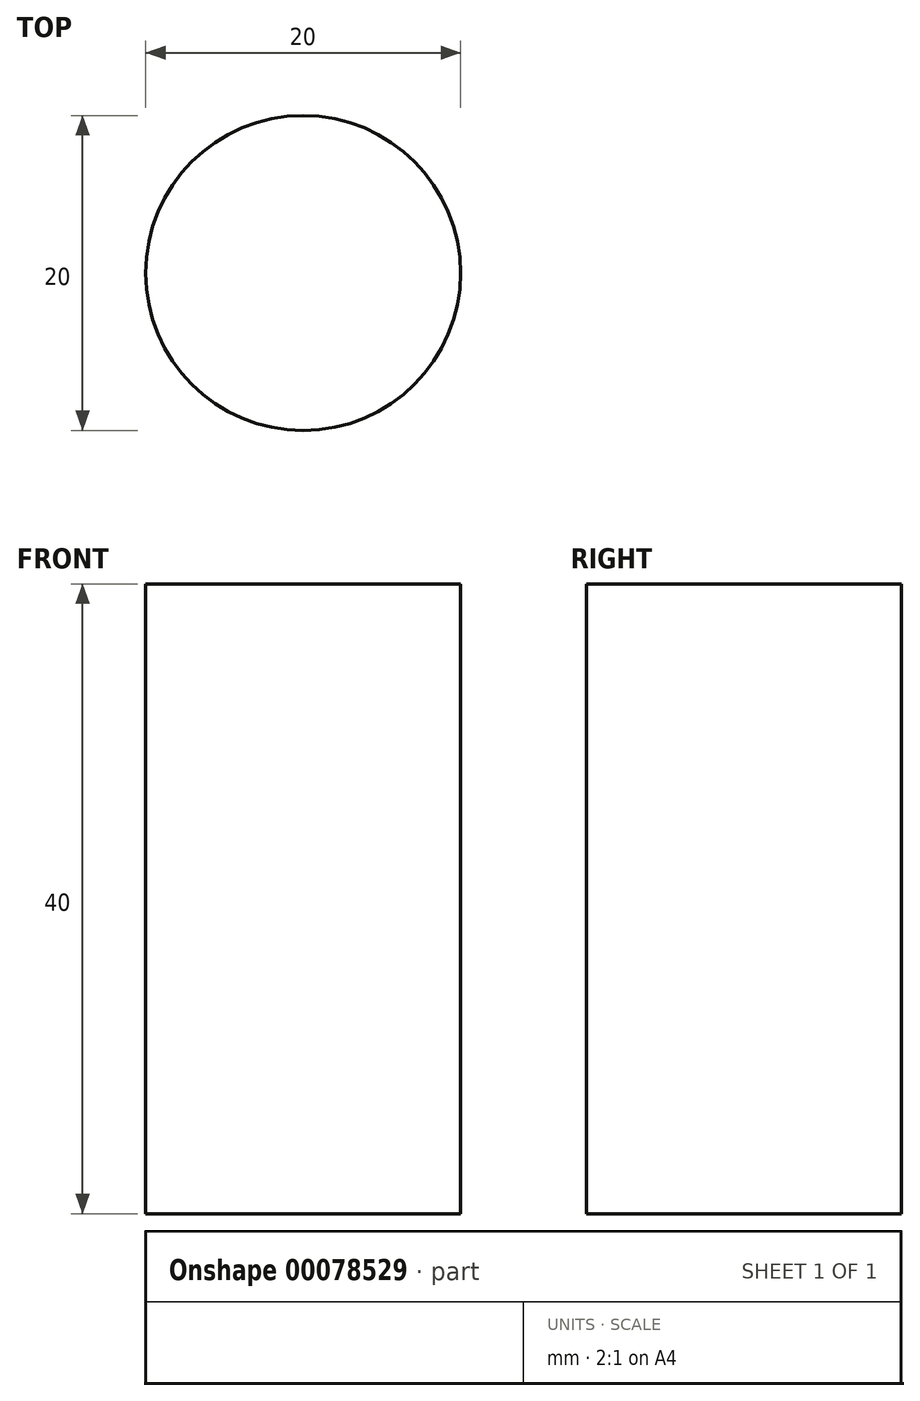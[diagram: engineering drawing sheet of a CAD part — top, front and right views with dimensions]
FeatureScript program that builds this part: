
annotation { "Feature Type Name" : "Feature", "Feature Type Description" : "" }
export const myFeature = defineFeature(function(context is Context, id is Id, definition is map)
    precondition{}
    {
        {
            var Q0;
            Q0=qCreatedBy(makeId("Right.planeOp"),FACE);
            var sketch = newSketch(context, id + "F0", { "sketchPlane" : qUnion([Q0])});
            skLineSegment(sketch, "E0.bottom", {"start": v(0, 40) * mm, "end": v(10, 40) * mm});
            skLineSegment(sketch, "E0.top", {"start": v(0, 0) * mm, "end": v(10, 0) * mm});
            skLineSegment(sketch, "E0.left", {"start": v(0, 40) * mm, "end": v(0, 0) * mm});
            skLineSegment(sketch, "E0.right", {"start": v(10, 40) * mm, "end": v(10, 0) * mm});
            skLineSegment(sketch, "E1", {"start": v(0, -47.53) * mm, "end": v(0, 107.75) * mm, "construction": true});
            skSolve(sketch);
        }
        {
            var Q0;
            Q0=makeQuery(id+"F0.imprint","IMPRINT",FACE,{"disambiguationData":[TD([[makeQuery(id+"F0.imprint","IMPRINT",EDGE,{"derivedFrom":sQuery(id+"F0.wireOp",EDGE,"E0.bottom")}),-1.0]])]});
            var Q1;
            Q1=sQuery(id+"F0.wireOp",EDGE,"E1");
            revolve(context, id + "F1", {"entities" : qUnion([Q0]), "axis" : qUnion([Q1]), "revolveType" : RevolveType.FULL});
        }
    });
